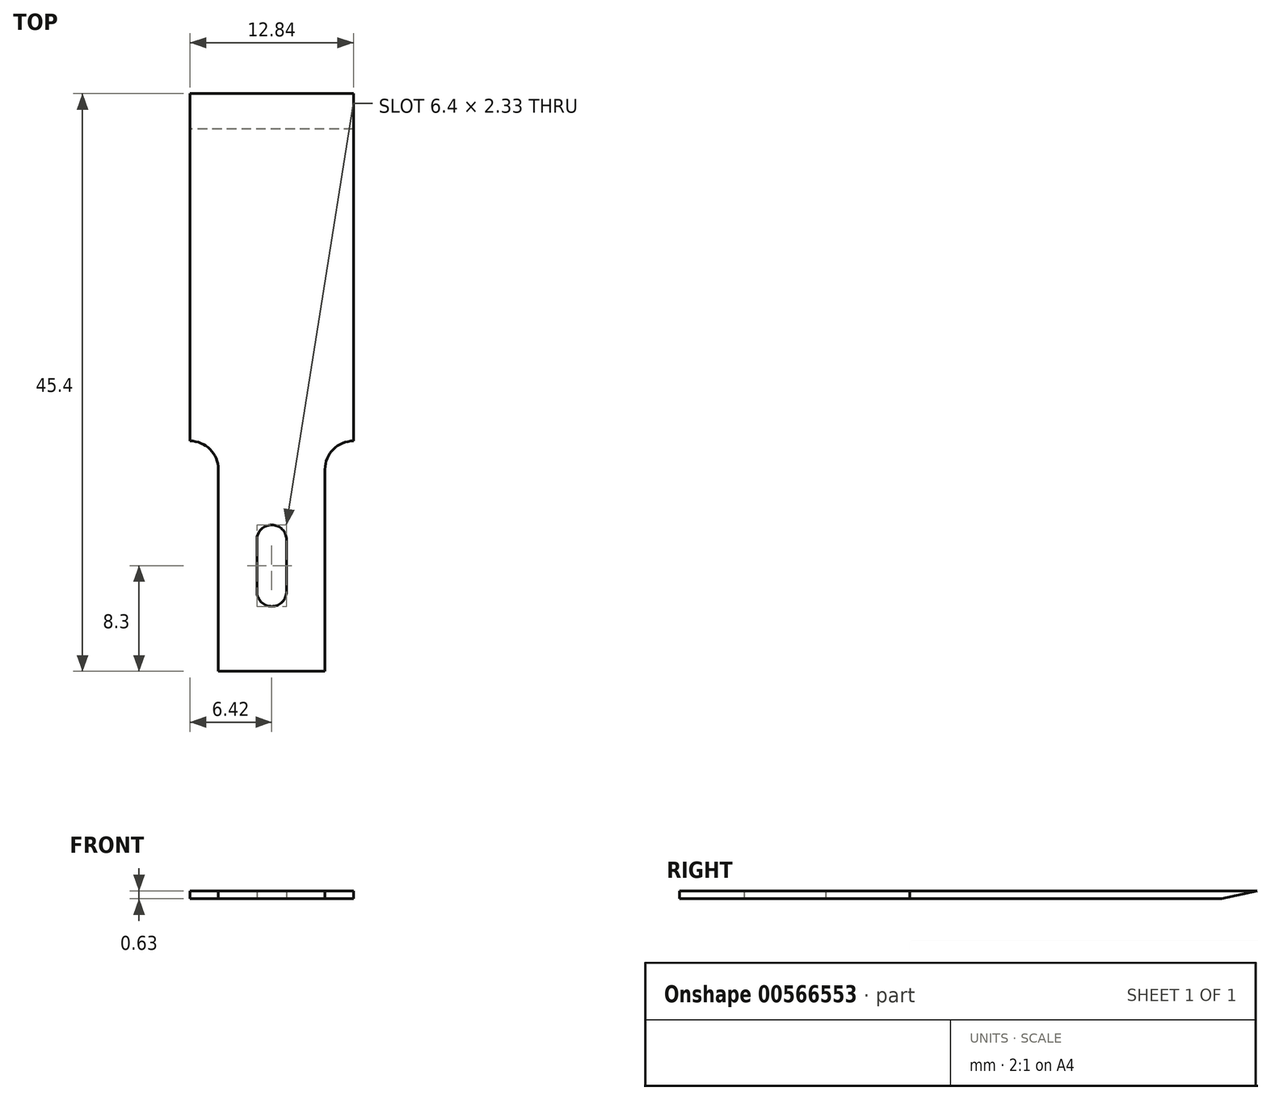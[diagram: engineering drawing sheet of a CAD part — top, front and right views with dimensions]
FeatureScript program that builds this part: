
annotation { "Feature Type Name" : "Feature", "Feature Type Description" : "" }
export const myFeature = defineFeature(function(context is Context, id is Id, definition is map)
    precondition{}
    {
        {
            var Q0;
            Q0=qCreatedBy(makeId("Top.planeOp"),FACE);
            var sketch = newSketch(context, id + "F0", { "sketchPlane" : qUnion([Q0])});
            skLineSegment(sketch, "E0", {"start": v(-6.42, 0) * mm, "end": v(6.42, 0) * mm});
            skLineSegment(sketch, "E1", {"start": v(6.42, 0) * mm, "end": v(6.42, -27.3) * mm});
            skLineSegment(sketch, "E2", {"start": v(6.42, -27.3) * mm, "end": v(60.6, -27.3) * mm, "construction": true});
            skLineSegment(sketch, "E3", {"start": v(-4.19, -45.4) * mm, "end": v(4.19, -45.4) * mm});
            skLineSegment(sketch, "E4", {"start": v(4.19, -45.4) * mm, "end": v(4.19, -29.53) * mm});
            skArc(sketch, "E5", {"start": v(4.19, -29.53) * mm, "mid": v(4.84, -27.95) * mm, "end": v(6.43, -27.3) * mm});
            skLineSegment(sketch, "E6", {"start": v(0, 0) * mm, "end": v(0, -45.4) * mm, "construction": true});
            skLineSegment(sketch, "E7.MirrorCS", {"start": v(-6.42, 0) * mm, "end": v(-6.42, -27.3) * mm});
            skArc(sketch, "E8.MirrorCS", {"start": v(-4.19, -29.53) * mm, "mid": v(-4.84, -27.95) * mm, "end": v(-6.42, -27.3) * mm});
            skLineSegment(sketch, "E9.MirrorCS", {"start": v(-4.19, -45.4) * mm, "end": v(-4.19, -29.53) * mm});
            skLineSegment(sketch, "E10", {"start": v(0, -39.14) * mm, "end": v(0, -35.06) * mm, "construction": true});
            skArc(sketch, "E11.0.startCap", {"start": v(1.17, -39.14) * mm, "mid": v(0, -40.3) * mm, "end": v(-1.16, -39.14) * mm});
            skArc(sketch, "E11.0.endCap", {"start": v(-1.16, -35.06) * mm, "mid": v(0, -33.9) * mm, "end": v(1.16, -35.06) * mm});
            skLineSegment(sketch, "E11.0.left", {"start": v(-1.16, -39.14) * mm, "end": v(-1.16, -35.06) * mm});
            skLineSegment(sketch, "E11.0.right", {"start": v(1.16, -39.14) * mm, "end": v(1.16, -35.06) * mm});
            skLineSegment(sketch, "E12", {"start": v(0, -40.3) * mm, "end": v(0, -39.14) * mm, "construction": true});
            skLineSegment(sketch, "E13", {"start": v(0, -33.9) * mm, "end": v(0, -40.3) * mm, "construction": true});
            skSolve(sketch);
        }
        {
            var Q0;
            Q0=makeQuery(id+"F0.imprint","IMPRINT",FACE,{"disambiguationData":[TD([[makeQuery(id+"F0.imprint","IMPRINT",EDGE,{"derivedFrom":sQuery(id+"F0.wireOp",EDGE,"E0")}),-1.0]])]});
            extrude(context, id + "F1", {"entities" : qUnion([Q0]), "depth" : .63 * mm, "offsetDistance" : 25.4 * mm});
        }
        {
            var Q0;
            Q0=makeQuery(id+"F1.opExtrude","SWEPT_FACE",FACE,{"disambiguationData":[OSD([sQuery(id+"F0.wireOp",EDGE,"E7.MirrorCS")])]});
            var sketch = newSketch(context, id + "F2", { "sketchPlane" : qUnion([Q0])});
            skLineSegment(sketch, "E14", {"start": v(0, 0) * mm, "end": v(0, 0.63) * mm});
            skLineSegment(sketch, "E15", {"start": v(0, 0.63) * mm, "end": v(2.78, 0) * mm});
            skLineSegment(sketch, "E16", {"start": v(2.78, 0) * mm, "end": v(0, 0) * mm});
            skSolve(sketch);
        }
        {
            var Q0;
            Q0=makeQuery(id+"F2.imprint","IMPRINT",FACE,{"disambiguationData":[TD([[makeQuery(id+"F2.imprint","IMPRINT",EDGE,{"derivedFrom":sQuery(id+"F2.wireOp",EDGE,"E14")}),1.0]])]});
            extrude(context, id + "F3", {"entities" : qUnion([Q0]), "operationType" : NewBodyOperationType.REMOVE, "endBound" : BoundingType.THROUGH_ALL, "oppositeDirection" : true, "depth" : 25.4 * mm, "offsetDistance" : 25.4 * mm});
        }
    });
